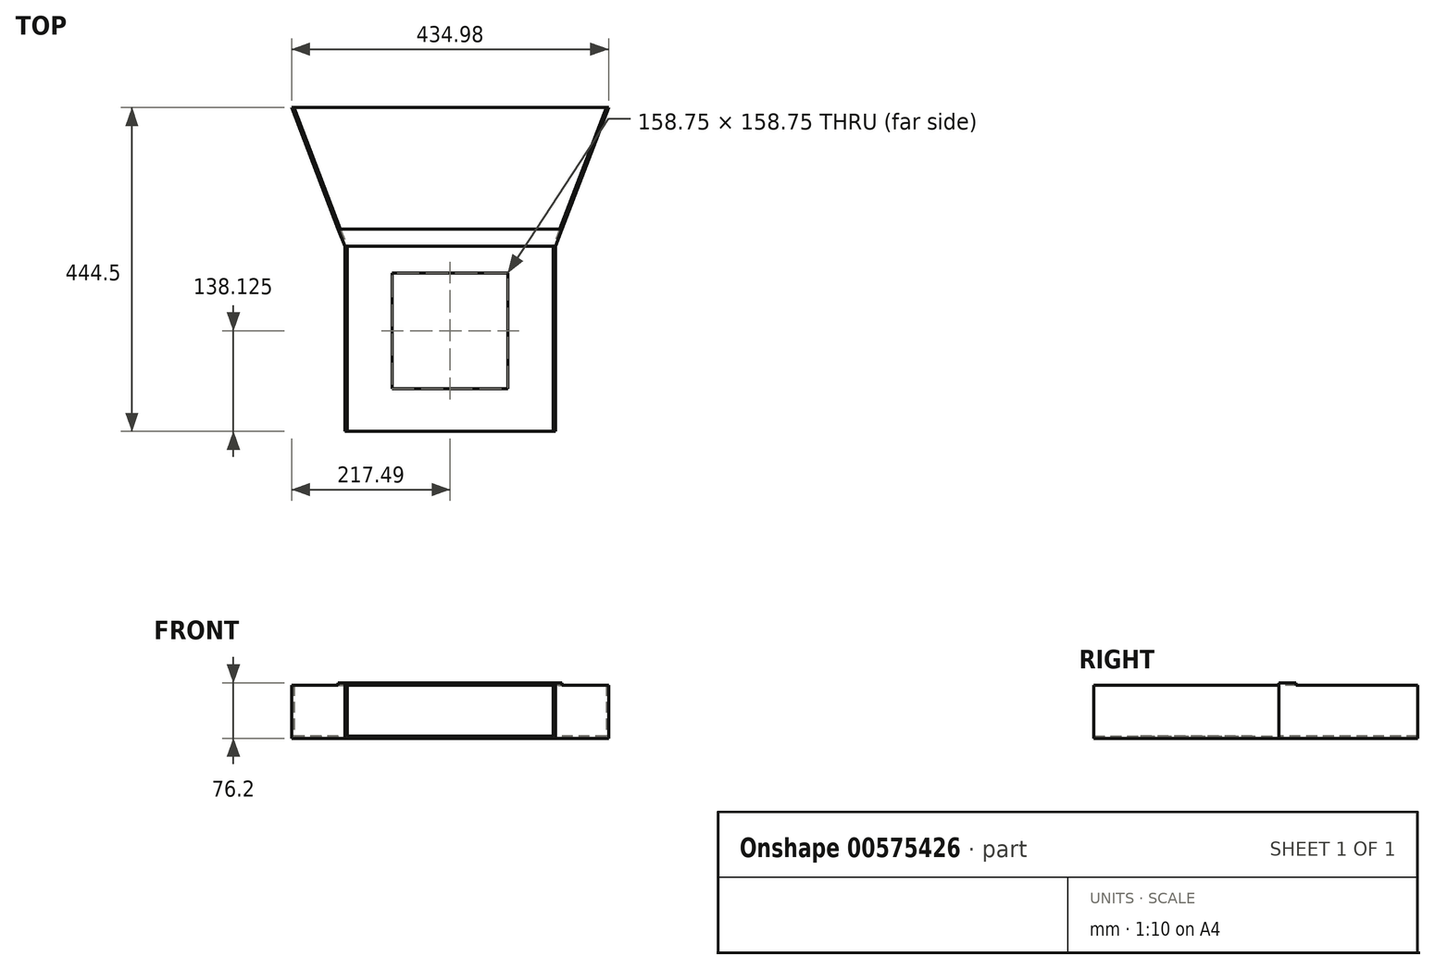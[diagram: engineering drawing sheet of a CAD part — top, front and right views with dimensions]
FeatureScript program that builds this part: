
annotation { "Feature Type Name" : "Feature", "Feature Type Description" : "" }
export const myFeature = defineFeature(function(context is Context, id is Id, definition is map)
    precondition{}
    {
        {
            var Q0;
            Q0=qCreatedBy(makeId("Top.planeOp"),FACE);
            var sketch = newSketch(context, id + "F0", { "sketchPlane" : qUnion([Q0])});
            skLineSegment(sketch, "E0.bottom", {"start": v(144.46, 95.25) * mm, "end": v(-144.46, 95.25) * mm});
            skLineSegment(sketch, "E0.top", {"start": v(144.46, -95.25) * mm, "end": v(-144.46, -95.25) * mm});
            skLineSegment(sketch, "E0.left", {"start": v(144.46, 95.25) * mm, "end": v(144.46, -95.25) * mm});
            skLineSegment(sketch, "E0.right", {"start": v(-144.46, 95.25) * mm, "end": v(-144.46, -95.25) * mm});
            skPoint(sketch, "E0.middle", {"position": v(0, 0) * mm});
            skSolve(sketch);
        }
        {
            var Q0;
            Q0=makeQuery(id+"F0.imprint","IMPRINT",FACE,{"disambiguationData":[TD([[makeQuery(id+"F0.imprint","IMPRINT",EDGE,{"derivedFrom":sQuery(id+"F0.wireOp",EDGE,"E0.bottom")}),1.0]])]});
            extrude(context, id + "F1", {"entities" : qUnion([Q0]), "depth" : 3.17 * mm, "offsetDistance" : 25.4 * mm});
        }
        {
            var Q0;
            Q0=makeQuery(id+"F1.opExtrude","CAP_FACE",FACE,{"disambiguationData":[OSD([sQuery(id+"F0.wireOp",EDGE,"E0.bottom"),sQuery(id+"F0.wireOp",EDGE,"E0.top"),sQuery(id+"F0.wireOp",EDGE,"E0.left"),sQuery(id+"F0.wireOp",EDGE,"E0.right")])],"isStart":false});
            var sketch = newSketch(context, id + "F2", { "sketchPlane" : qUnion([Q0])});
            skLineSegment(sketch, "E1", {"start": v(-144.46, 95.25) * mm, "end": v(-217.49, 95.25) * mm});
            skLineSegment(sketch, "E2", {"start": v(-217.49, 95.25) * mm, "end": v(-144.46, -95.25) * mm});
            skLineSegment(sketch, "E3", {"start": v(-144.46, -95.25) * mm, "end": v(-144.46, 95.25) * mm});
            skSolve(sketch);
        }
        {
            var Q0;
            Q0=makeQuery(id+"F2.imprint","IMPRINT",FACE,{"disambiguationData":[TD([[makeQuery(id+"F2.imprint","IMPRINT",EDGE,{"derivedFrom":sQuery(id+"F2.wireOp",EDGE,"E1")}),1.0]])]});
            extrude(context, id + "F3", {"entities" : qUnion([Q0]), "operationType" : NewBodyOperationType.ADD, "oppositeDirection" : true, "depth" : 3.17 * mm, "offsetDistance" : 25.4 * mm});
        }
        {
            var Q0;
            Q0=makeQuery(id+"F3.boolean.opBoolean","MERGE",FACE,{"derivedFrom":[makeQuery(id+"F1.opExtrude","CAP_FACE",FACE,{"disambiguationData":[OSD([sQuery(id+"F0.wireOp",EDGE,"E0.bottom"),sQuery(id+"F0.wireOp",EDGE,"E0.top"),sQuery(id+"F0.wireOp",EDGE,"E0.left"),sQuery(id+"F0.wireOp",EDGE,"E0.right")])],"isStart":true}),makeQuery(id+"F3.opExtrude","CAP_FACE",FACE,{"disambiguationData":[OSD([sQuery(id+"F2.wireOp",EDGE,"E1"),sQuery(id+"F2.wireOp",EDGE,"E2"),sQuery(id+"F2.wireOp",EDGE,"E3")])],"isStart":false})]});
            var sketch = newSketch(context, id + "F4", { "sketchPlane" : qUnion([Q0])});
            skLineSegment(sketch, "E4", {"start": v(144.46, 95.25) * mm, "end": v(144.46, -95.25) * mm});
            skLineSegment(sketch, "E5", {"start": v(144.46, -95.25) * mm, "end": v(217.49, -95.25) * mm});
            skLineSegment(sketch, "E6", {"start": v(217.49, -95.25) * mm, "end": v(144.46, 95.25) * mm});
            skSolve(sketch);
        }
        {
            var Q0;
            Q0=makeQuery(id+"F4.imprint","IMPRINT",FACE,{"disambiguationData":[TD([[makeQuery(id+"F4.imprint","IMPRINT",EDGE,{"derivedFrom":sQuery(id+"F4.wireOp",EDGE,"E4")}),-1.0]])]});
            extrude(context, id + "F5", {"entities" : qUnion([Q0]), "operationType" : NewBodyOperationType.ADD, "oppositeDirection" : true, "depth" : 3.17 * mm, "offsetDistance" : 25.4 * mm});
        }
        {
            var Q0;
            Q0=makeQuery(id+"F5.boolean.opBoolean","MERGE",FACE,{"derivedFrom":[makeQuery(id+"F3.boolean.opBoolean","MERGE",FACE,{"derivedFrom":[makeQuery(id+"F1.opExtrude","CAP_FACE",FACE,{"disambiguationData":[OSD([sQuery(id+"F0.wireOp",EDGE,"E0.bottom"),sQuery(id+"F0.wireOp",EDGE,"E0.top"),sQuery(id+"F0.wireOp",EDGE,"E0.left"),sQuery(id+"F0.wireOp",EDGE,"E0.right")])],"isStart":false}),makeQuery(id+"F3.opExtrude","CAP_FACE",FACE,{"disambiguationData":[OSD([sQuery(id+"F2.wireOp",EDGE,"E1"),sQuery(id+"F2.wireOp",EDGE,"E2"),sQuery(id+"F2.wireOp",EDGE,"E3")])],"isStart":true})]}),makeQuery(id+"F5.opExtrude","CAP_FACE",FACE,{"disambiguationData":[OSD([sQuery(id+"F4.wireOp",EDGE,"E4"),sQuery(id+"F4.wireOp",EDGE,"E5"),sQuery(id+"F4.wireOp",EDGE,"E6")])],"isStart":false})]});
            var sketch = newSketch(context, id + "F6", { "sketchPlane" : qUnion([Q0])});
            skLineSegment(sketch, "E7.bottom", {"start": v(-144.46, -95.25) * mm, "end": v(144.46, -95.25) * mm});
            skLineSegment(sketch, "E7.top", {"start": v(-144.46, -349.25) * mm, "end": v(144.46, -349.25) * mm});
            skLineSegment(sketch, "E7.left", {"start": v(-144.46, -95.25) * mm, "end": v(-144.46, -349.25) * mm});
            skLineSegment(sketch, "E7.right", {"start": v(144.46, -95.25) * mm, "end": v(144.46, -349.25) * mm});
            skSolve(sketch);
        }
        {
            var Q0;
            Q0=makeQuery(id+"F6.imprint","IMPRINT",FACE,{"disambiguationData":[TD([[makeQuery(id+"F6.imprint","IMPRINT",EDGE,{"derivedFrom":sQuery(id+"F6.wireOp",EDGE,"E7.bottom")}),1.0]])]});
            extrude(context, id + "F7", {"entities" : qUnion([Q0]), "operationType" : NewBodyOperationType.ADD, "oppositeDirection" : true, "depth" : 3.17 * mm, "offsetDistance" : 25.4 * mm});
        }
        {
            var Q0;
            Q0=makeQuery(id+"F7.boolean.opBoolean","MERGE",FACE,{"derivedFrom":[makeQuery(id+"F5.boolean.opBoolean","MERGE",FACE,{"derivedFrom":[makeQuery(id+"F3.boolean.opBoolean","MERGE",FACE,{"derivedFrom":[makeQuery(id+"F1.opExtrude","CAP_FACE",FACE,{"disambiguationData":[OSD([sQuery(id+"F0.wireOp",EDGE,"E0.bottom"),sQuery(id+"F0.wireOp",EDGE,"E0.top"),sQuery(id+"F0.wireOp",EDGE,"E0.left"),sQuery(id+"F0.wireOp",EDGE,"E0.right")])],"isStart":false}),makeQuery(id+"F3.opExtrude","CAP_FACE",FACE,{"disambiguationData":[OSD([sQuery(id+"F2.wireOp",EDGE,"E1"),sQuery(id+"F2.wireOp",EDGE,"E2"),sQuery(id+"F2.wireOp",EDGE,"E3")])],"isStart":true})]}),makeQuery(id+"F5.opExtrude","CAP_FACE",FACE,{"disambiguationData":[OSD([sQuery(id+"F4.wireOp",EDGE,"E4"),sQuery(id+"F4.wireOp",EDGE,"E5"),sQuery(id+"F4.wireOp",EDGE,"E6")])],"isStart":false})]}),makeQuery(id+"F7.opExtrude","CAP_FACE",FACE,{"disambiguationData":[OSD([sQuery(id+"F6.wireOp",EDGE,"E7.bottom"),sQuery(id+"F6.wireOp",EDGE,"E7.top"),sQuery(id+"F6.wireOp",EDGE,"E7.left"),sQuery(id+"F6.wireOp",EDGE,"E7.right")])],"isStart":true})]});
            var sketch = newSketch(context, id + "F8", { "sketchPlane" : qUnion([Q0])});
            skLineSegment(sketch, "E8.bottom", {"start": v(79.37, -131.75) * mm, "end": v(-79.38, -131.75) * mm});
            skLineSegment(sketch, "E8.top", {"start": v(79.38, -290.5) * mm, "end": v(-79.37, -290.5) * mm});
            skLineSegment(sketch, "E8.left", {"start": v(79.37, -131.75) * mm, "end": v(79.38, -290.5) * mm});
            skLineSegment(sketch, "E8.right", {"start": v(-79.38, -131.75) * mm, "end": v(-79.37, -290.5) * mm});
            skPoint(sketch, "E8.middle", {"position": v(0, -211.12) * mm});
            skSolve(sketch);
        }
        {
            var Q0;
            Q0=makeQuery(id+"F8.imprint","IMPRINT",FACE,{"disambiguationData":[TD([[makeQuery(id+"F8.imprint","IMPRINT",EDGE,{"derivedFrom":sQuery(id+"F8.wireOp",EDGE,"E8.bottom")}),1.0]])]});
            extrude(context, id + "F9", {"entities" : qUnion([Q0]), "operationType" : NewBodyOperationType.REMOVE, "oppositeDirection" : true, "depth" : 3.17 * mm, "offsetDistance" : 25.4 * mm});
        }
        {
            var Q0;
            Q0=makeQuery(id+"F7.boolean.opBoolean","MERGE",FACE,{"derivedFrom":[makeQuery(id+"F5.boolean.opBoolean","MERGE",FACE,{"derivedFrom":[makeQuery(id+"F3.boolean.opBoolean","MERGE",FACE,{"derivedFrom":[makeQuery(id+"F1.opExtrude","CAP_FACE",FACE,{"disambiguationData":[OSD([sQuery(id+"F0.wireOp",EDGE,"E0.bottom"),sQuery(id+"F0.wireOp",EDGE,"E0.top"),sQuery(id+"F0.wireOp",EDGE,"E0.left"),sQuery(id+"F0.wireOp",EDGE,"E0.right")])],"isStart":false}),makeQuery(id+"F3.opExtrude","CAP_FACE",FACE,{"disambiguationData":[OSD([sQuery(id+"F2.wireOp",EDGE,"E1"),sQuery(id+"F2.wireOp",EDGE,"E2"),sQuery(id+"F2.wireOp",EDGE,"E3")])],"isStart":true})]}),makeQuery(id+"F5.opExtrude","CAP_FACE",FACE,{"disambiguationData":[OSD([sQuery(id+"F4.wireOp",EDGE,"E4"),sQuery(id+"F4.wireOp",EDGE,"E5"),sQuery(id+"F4.wireOp",EDGE,"E6")])],"isStart":false})]}),makeQuery(id+"F7.opExtrude","CAP_FACE",FACE,{"disambiguationData":[OSD([sQuery(id+"F6.wireOp",EDGE,"E7.bottom"),sQuery(id+"F6.wireOp",EDGE,"E7.top"),sQuery(id+"F6.wireOp",EDGE,"E7.left"),sQuery(id+"F6.wireOp",EDGE,"E7.right")])],"isStart":true})]});
            var sketch = newSketch(context, id + "F10", { "sketchPlane" : qUnion([Q0])});
            skLineSegment(sketch, "E9.bottom", {"start": v(-217.49, 95.25) * mm, "end": v(-214.31, 95.25) * mm});
            skLineSegment(sketch, "E9.top", {"start": v(-144.46, -95.25) * mm, "end": v(-141.29, -95.25) * mm});
            skLineSegment(sketch, "E9.left", {"start": v(-217.49, 95.25) * mm, "end": v(-144.46, -95.25) * mm});
            skLineSegment(sketch, "E9.right", {"start": v(-214.31, 95.25) * mm, "end": v(-141.29, -95.25) * mm});
            skSolve(sketch);
        }
        {
            var Q0;
            Q0=makeQuery(id+"F10.imprint","IMPRINT",FACE,{"disambiguationData":[TD([[makeQuery(id+"F10.imprint","IMPRINT",EDGE,{"derivedFrom":sQuery(id+"F10.wireOp",EDGE,"E9.top")}),-1.0]])]});
            var sketch = newSketch(context, id + "F11", { "sketchPlane" : qUnion([Q0])});
            skLineSegment(sketch, "E10.bottom", {"start": v(217.49, 95.25) * mm, "end": v(214.31, 95.25) * mm});
            skLineSegment(sketch, "E10.top", {"start": v(144.46, -95.25) * mm, "end": v(141.29, -95.25) * mm});
            skLineSegment(sketch, "E10.left", {"start": v(217.49, 95.25) * mm, "end": v(144.46, -95.25) * mm});
            skLineSegment(sketch, "E10.right", {"start": v(214.31, 95.25) * mm, "end": v(141.29, -95.25) * mm});
            skSolve(sketch);
        }
        {
            var Q0;
            Q0=makeQuery(id+"F10.imprint","IMPRINT",FACE,{"disambiguationData":[TD([[makeQuery(id+"F10.imprint","IMPRINT",EDGE,{"derivedFrom":sQuery(id+"F10.wireOp",EDGE,"E9.bottom")}),1.0]])]});
            var Q1;
            Q1=makeQuery(id+"F11.imprint","IMPRINT",FACE,{"disambiguationData":[TD([[makeQuery(id+"F11.imprint","IMPRINT",EDGE,{"derivedFrom":sQuery(id+"F11.wireOp",EDGE,"E10.bottom")}),1.0]])]});
            extrude(context, id + "F12", {"entities" : qUnion([Q0, Q1]), "operationType" : NewBodyOperationType.ADD, "depth" : 69.85 * mm, "offsetDistance" : 25.4 * mm});
        }
        {
            var Q0;
            Q0=makeQuery(id+"F7.boolean.opBoolean","MERGE",FACE,{"derivedFrom":[makeQuery(id+"F5.boolean.opBoolean","MERGE",FACE,{"derivedFrom":[makeQuery(id+"F3.boolean.opBoolean","MERGE",FACE,{"derivedFrom":[makeQuery(id+"F1.opExtrude","CAP_FACE",FACE,{"disambiguationData":[OSD([sQuery(id+"F0.wireOp",EDGE,"E0.bottom"),sQuery(id+"F0.wireOp",EDGE,"E0.top"),sQuery(id+"F0.wireOp",EDGE,"E0.left"),sQuery(id+"F0.wireOp",EDGE,"E0.right")])],"isStart":false}),makeQuery(id+"F3.opExtrude","CAP_FACE",FACE,{"disambiguationData":[OSD([sQuery(id+"F2.wireOp",EDGE,"E1"),sQuery(id+"F2.wireOp",EDGE,"E2"),sQuery(id+"F2.wireOp",EDGE,"E3")])],"isStart":true})]}),makeQuery(id+"F5.opExtrude","CAP_FACE",FACE,{"disambiguationData":[OSD([sQuery(id+"F4.wireOp",EDGE,"E4"),sQuery(id+"F4.wireOp",EDGE,"E5"),sQuery(id+"F4.wireOp",EDGE,"E6")])],"isStart":false})]}),makeQuery(id+"F7.opExtrude","CAP_FACE",FACE,{"disambiguationData":[OSD([sQuery(id+"F6.wireOp",EDGE,"E7.bottom"),sQuery(id+"F6.wireOp",EDGE,"E7.top"),sQuery(id+"F6.wireOp",EDGE,"E7.left"),sQuery(id+"F6.wireOp",EDGE,"E7.right")])],"isStart":true})]});
            var sketch = newSketch(context, id + "F13", { "sketchPlane" : qUnion([Q0])});
            skLineSegment(sketch, "E11.bottom", {"start": v(-144.46, -349.25) * mm, "end": v(-141.29, -349.25) * mm});
            skLineSegment(sketch, "E11.top", {"start": v(-144.46, -95.25) * mm, "end": v(-141.29, -95.25) * mm});
            skLineSegment(sketch, "E11.left", {"start": v(-144.46, -349.25) * mm, "end": v(-144.46, -95.25) * mm});
            skLineSegment(sketch, "E11.right", {"start": v(-141.29, -349.25) * mm, "end": v(-141.29, -95.25) * mm});
            skLineSegment(sketch, "E12.bottom", {"start": v(144.46, -349.25) * mm, "end": v(141.29, -349.25) * mm});
            skLineSegment(sketch, "E12.top", {"start": v(144.46, -95.25) * mm, "end": v(141.29, -95.25) * mm});
            skLineSegment(sketch, "E12.left", {"start": v(144.46, -349.25) * mm, "end": v(144.46, -95.25) * mm});
            skLineSegment(sketch, "E12.right", {"start": v(141.29, -349.25) * mm, "end": v(141.29, -95.25) * mm});
            skSolve(sketch);
        }
        {
            var Q0;
            Q0=makeQuery(id+"F13.imprint","IMPRINT",FACE,{"disambiguationData":[TD([[makeQuery(id+"F13.imprint","IMPRINT",EDGE,{"derivedFrom":sQuery(id+"F13.wireOp",EDGE,"E11.bottom")}),1.0]])]});
            var Q1;
            Q1=makeQuery(id+"F13.imprint","IMPRINT",FACE,{"disambiguationData":[TD([[makeQuery(id+"F13.imprint","IMPRINT",EDGE,{"derivedFrom":sQuery(id+"F13.wireOp",EDGE,"E12.bottom")}),1.0]])]});
            extrude(context, id + "F14", {"entities" : qUnion([Q0, Q1]), "operationType" : NewBodyOperationType.ADD, "depth" : 69.85 * mm, "offsetDistance" : 25.4 * mm});
        }
        {
            var Q0;
            Q0=makeQuery(id+"F14.boolean.opBoolean","MERGE",FACE,{"derivedFrom":[makeQuery(id+"F12.opExtrude","CAP_FACE",FACE,{"disambiguationData":[OSD([sQuery(id+"F10.wireOp",EDGE,"E9.bottom"),sQuery(id+"F10.wireOp",EDGE,"E9.top"),sQuery(id+"F10.wireOp",EDGE,"E9.left"),sQuery(id+"F10.wireOp",EDGE,"E9.right")])],"isStart":false}),makeQuery(id+"F14.opExtrude","CAP_FACE",FACE,{"disambiguationData":[OSD([sQuery(id+"F13.wireOp",EDGE,"E11.bottom"),sQuery(id+"F13.wireOp",EDGE,"E11.top"),sQuery(id+"F13.wireOp",EDGE,"E11.left"),sQuery(id+"F13.wireOp",EDGE,"E11.right")])],"isStart":false})]});
            var sketch = newSketch(context, id + "F15", { "sketchPlane" : qUnion([Q0])});
            skLineSegment(sketch, "E13", {"start": v(-144.46, -95.25) * mm, "end": v(-153.55, -71.53) * mm});
            skLineSegment(sketch, "E14", {"start": v(-153.55, -71.53) * mm, "end": v(153.55, -71.53) * mm});
            skLineSegment(sketch, "E15", {"start": v(153.55, -71.53) * mm, "end": v(144.46, -95.25) * mm});
            skLineSegment(sketch, "E16", {"start": v(-144.46, -95.25) * mm, "end": v(144.46, -95.25) * mm});
            skSolve(sketch);
        }
        {
            var Q0;
            {var subQ0=sQuery(id+"F15.wireOp",EDGE,"E13");Q0=makeQuery(id+"F15.imprint","IMPRINT",FACE,{"disambiguationData":[TD([[makeQuery(id+"F15.imprint","IMPRINT",EDGE,{"derivedFrom":subQ0}),1.0]])]});}
            var Q1;
            {var subQ0=sQuery(id+"F15.wireOp",EDGE,"E15");Q1=makeQuery(id+"F15.imprint","IMPRINT",FACE,{"disambiguationData":[TD([[makeQuery(id+"F15.imprint","IMPRINT",EDGE,{"derivedFrom":subQ0}),-1.0]])]});}
            extrude(context, id + "F16", {"entities" : qUnion([Q0, Q1]), "operationType" : NewBodyOperationType.ADD, "depth" : 3.17 * mm, "offsetDistance" : 25.4 * mm});
        }
    });
